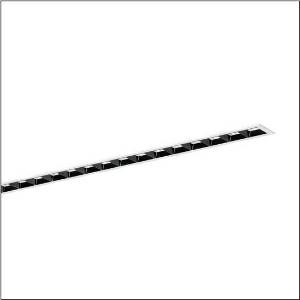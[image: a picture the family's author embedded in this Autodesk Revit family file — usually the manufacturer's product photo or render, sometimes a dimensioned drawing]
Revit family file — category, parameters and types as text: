
# Revit family: silica_21_51mx12tat4w
name_source: partatom
category: Lighting Fixtures
units: mm (PartAtom-declared; Revit-internal decimal feet)

## family parameters
Cut with Voids When Loaded = No
Host = Face
Light Source = No
Part Type = Normal
Room Calculation Point = No
Round Connector Dimension = Use Diameter
Shared = No

## types (1)
- --- (1 x LED, 3720 lm, 32.1 W, 6500K)
    Apparent Load = 32 VA
    CIE Flux Codes = 84 100 100 100 100
    Color Rendering = 80
    Color Temperature = 6500K
    Default Elevation = 1800 mm
    Description = Silica 21, office luminaire, primary light control with darklight reflector, of PMMA, black, CAT 2 (L<= 3000cd/m²), light emission: direct distribution, primary light characteristic: symmetric, installation type: recessed, LED, rated luminous flux: 3.720lm, luminous efficacy: 110lm/W, light colour: 8tw, colour temperature: 2700..6500K, control gear: DALI DT8, with terminal, 3+2-pole, max. 2.5mm², mains connection: 220..240V, AC, 50/60Hz, rated input power: 33.8W, luminaire housing, of aluminium, traffic white (RAL 9016), length: 1.228mm, width: 79mm, height: 53mm, protection rating (complete): IP20, insulation class (complete): insulation class I (protective earthing), certification: CE, ENEC, VDE, permissible operating ambient temperature: 0..+35°C, standard: EN 50419, packaging unit: 1 piece
    Height = 0 mm  [stored 0 ft]
    Lamp = 1 x LED
    Lamp Light Flux = 3720 lm
    Lamp Power = 32.1 W
    Lamp count = 1
    Length = 1227 mm
    Luminous efficacy = 116 lm/W
    Manufacturer = Siteco
    ModVariant = No
    Model = 51MX12TAT4W
    Mounting Place = Ceiling
    Mounting Type = Recessed
    Number of Poles = 1
    OnlyDefault = Yes
    Power Factor = 1
    Product Name = Silica 21
    Product group = office luminaire | ceiling recessed
    ProductGroupID = 400
    Protection Class = Protection class I
    Protection Degree = IP 20
    RLX_Detail_Level = 1
    RLX_Emergency_Light_Flux = 0 lm
    RLX_Emergency_Type = 0
    RLX_Emergency_Type_DB = No
    RlxData = <blob elided: 35749 chars, md5=4058aa41>
    Socket = socket
    Standby Power = 0 W
    System Light Flux = 3720 lm
    System Power = 32 W
    Type Comments = individual setting
    Type Image = l_1335880.jpg
    URL = http://relux.com
    VarID = @adj_139673
    Voltage = 0 V
    Weight = 0.00 kg
    Width = 79 mm

note: [stored X ft] marks values corroborated as IEEE doubles in the binary element streams (Revit-internal decimal feet)

## geometry (parser evidence)
native form markers: Blend x4, Sweep x10
no freeform markers — native parametric forms only
